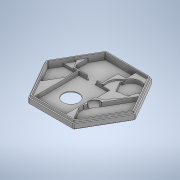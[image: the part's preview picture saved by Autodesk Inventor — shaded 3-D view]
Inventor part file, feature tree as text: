
AUTODESK INVENTOR PART (.ipt)
format: ipt  version: 2021 (Build 250183000, 183)  size: 617,472 bytes
history: native  units: mm
features: extrude x8, projected_geometry x6, sketch x5, other x2, plane x1, loft x1, fillet x1, chamfer x1
ambient origin geometry x8: Origin, YZ Plane, XZ Plane, XY Plane, X Axis, Y Axis, Z Axis, Center Point
bodies: Solid1 (feature_tree)
feature tree (25):
  extrude  "Extrusion1"  Depth=0.2mm
  extrude  "Extrusion2"  Depth=9.2mm TaperAngle=0.0deg
  extrude  "Extrusion3"  Depth=108.4mm
  extrude  "Extrusion4"  Depth=43.0mm
  extrude  "Extrusion5"  Depth=2.0mm
  extrude  "Extrusion6"  Depth=2.0mm
  extrude  "Extrusion8"  Depth=1.5mm
  extrude  "Extrusion9"  Depth=1.5mm
  plane  "Work Plane1"
  loft  "Loft1"
  fillet  "Fillet2"  Radius=6.2mm
  chamfer  "Chamfer1"  [1 undecoded]
  sketch  "Sketch2"  dims[d0=102.0mm d2=0.2mm]
  projected_geometry  "Projected Loop1"
  sketch  "Sketch3"  dims[d8=1.0mm d9=0.0mm d10=9.2mm d11=0.0mm]
  projected_geometry  "Projected Loop2"
  sketch  "Sketch5"  dims[d16=108.4mm d17=42.0mm]
  projected_geometry  "Projected Loop4"
  sketch  "Sketch7"  dims[d18=64.0mm d19=43.0mm]
  projected_geometry  "Projected Loop6"
  sketch  "Sketch9"  dims[d21=24.8mm d22=21.8mm d26=65.0mm d27=1.5mm d28=1.5mm d29=1.5mm d30=6.2mm d31=0.0mm d32=5.5mm d33=0.0mm d36=25.25mm d37=0.5mm d38=31.7mm d39=0.5mm d41=24.8mm d42=21.8mm d43=0.5mm d44=1.0mm d45=0.5mm d46=0.25mm d47=0.5mm d50=35.5mm d54=45.0deg d55=2.0mm d56=1.0mm d67=0.5mm d74=0.5mm d77=0.5mm d78=0.5mm d79=0.5mm d80=0.5mm d81=0.5mm d83=0.5mm d84=0.5mm d85=1.5mm d86=45.0deg d87=2.0mm d88=12.5mm d89=20.9mm d90=0.5mm d91=1.5mm d92=0.5mm d93=0.5mm d94=0.5mm d95=0.5mm d96=0.5mm d97=0.5mm d98=0.5mm d99=0.5mm d100=0.5mm d102=1.5mm d103=0.5mm d105=2.0mm d106=0.0mm d109=0.5mm d110=1.0mm d111=1.5mm d112=1.0mm d113=25.25mm d114=16.4mm d115=0.5mm d116=7.2mm d117=22.0mm d118=10.0mm d121=10.0mm d122=0.0mm d126=10.0mm d127=0.5mm d128=0.0mm d132=0.5mm d133=0.5mm d134=0.5mm d135=0.75mm d136=8.5mm d137=0.5mm d138=0.0mm d140=6.5mm d141=0.0mm d142=90.0deg d143=0.0mm d144=90.0deg d145=0.0mm d146=90.0deg d147=0.5mm d148=2.0mm d149=1.0mm d150=2.0mm d151=45.0deg]
  projected_geometry  "Projected Loop8"
  projected_geometry  "Projected Loop9"
  other  "Edges1"
  other  "Edges2"
note: 1 required parameter value undecoded (feature->parameter linkage not recoverable at this tier; creation-order binding heuristic only, values carry confidence <= 0.55)
